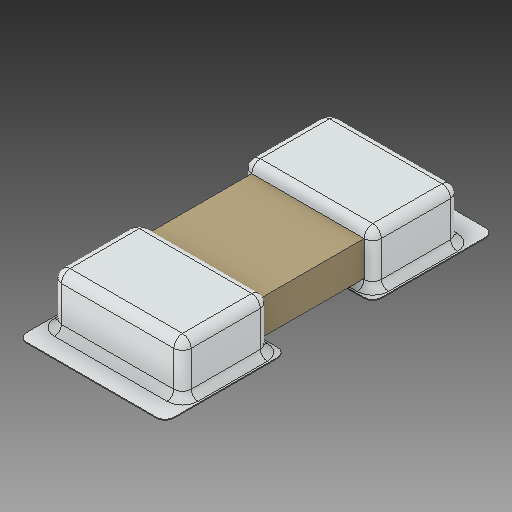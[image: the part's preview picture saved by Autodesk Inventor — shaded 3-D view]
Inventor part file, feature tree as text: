
AUTODESK INVENTOR PART (.ipt)
format: ipt  version: 2019.4 (Build 234330000, 330)  size: 172,544 bytes
history: native  units: mm
features: fillet x1
ambient origin geometry x8: Origin, YZ Plane, XZ Plane, XY Plane, X Axis, Y Axis, Z Axis, Center Point
bodies: Solid1 (feature_tree)
feature tree (1):
  fillet  "Fillet2"  [1 undecoded]
note: 1 required parameter value undecoded (feature->parameter linkage not recoverable at this tier; creation-order binding heuristic only, values carry confidence <= 0.55)
